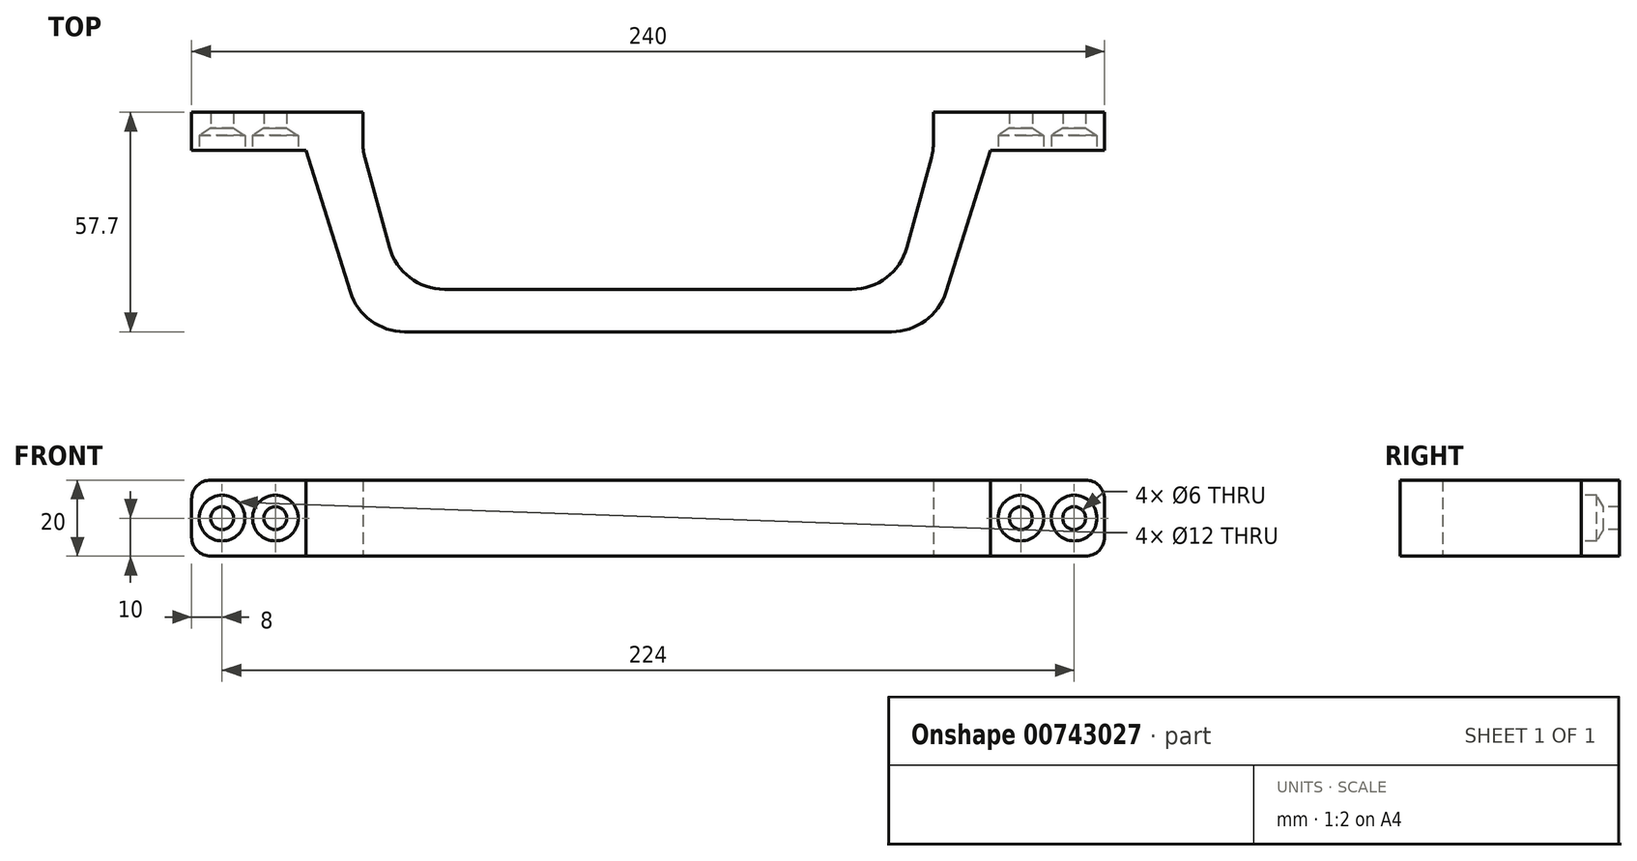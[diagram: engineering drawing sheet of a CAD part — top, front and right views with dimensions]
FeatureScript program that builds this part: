
annotation { "Feature Type Name" : "Feature", "Feature Type Description" : "" }
export const myFeature = defineFeature(function(context is Context, id is Id, definition is map)
    precondition{}
    {
        {
            var Q0;
            Q0=qCreatedBy(makeId("Top.planeOp"),FACE);
            var sketch = newSketch(context, id + "F0", { "sketchPlane" : qUnion([Q0])});
            skLineSegment(sketch, "E0.bottom", {"start": v(-120, 5) * mm, "end": v(120, 5) * mm});
            skLineSegment(sketch, "E0.top", {"start": v(-120, -5) * mm, "end": v(120, -5) * mm});
            skLineSegment(sketch, "E0.left", {"start": v(-120, 5) * mm, "end": v(-120, -5) * mm});
            skLineSegment(sketch, "E0.right", {"start": v(120, 5) * mm, "end": v(120, -5) * mm});
            skPoint(sketch, "E0.middle", {"position": v(0, 0) * mm});
            skLineSegment(sketch, "E1", {"start": v(-90, 5) * mm, "end": v(-90, -5) * mm});
            skLineSegment(sketch, "E2", {"start": v(90, -5) * mm, "end": v(90, 5) * mm});
            skLineSegment(sketch, "E3", {"start": v(-75, 5) * mm, "end": v(-75, -5) * mm});
            skLineSegment(sketch, "E4", {"start": v(75, 5) * mm, "end": v(75, -5) * mm});
            skLineSegment(sketch, "E5", {"start": v(-90, -5) * mm, "end": v(-75, -52.7) * mm});
            skLineSegment(sketch, "E6", {"start": v(-75, -52.7) * mm, "end": v(75, -52.7) * mm});
            skLineSegment(sketch, "E7", {"start": v(75, -52.7) * mm, "end": v(90, -5) * mm});
            skLineSegment(sketch, "E8", {"start": v(-75, -5) * mm, "end": v(-65, -41.52) * mm});
            skLineSegment(sketch, "E9", {"start": v(-65, -41.52) * mm, "end": v(65, -41.52) * mm});
            skLineSegment(sketch, "E10", {"start": v(65, -41.52) * mm, "end": v(75, -5) * mm});
            skSolve(sketch);
        }
        {
            var Q0;
            {var subQ0=sQuery(id+"F0.wireOp",EDGE,"E0.left");Q0=makeQuery(id+"F0.imprint","IMPRINT",FACE,{"disambiguationData":[TD([[makeQuery(id+"F0.imprint","IMPRINT",EDGE,{"derivedFrom":subQ0}),1.0]])]});}
            var Q1;
            {var subQ0=sQuery(id+"F0.wireOp",EDGE,"E1");Q1=makeQuery(id+"F0.imprint","IMPRINT",FACE,{"disambiguationData":[TD([[makeQuery(id+"F0.imprint","IMPRINT",EDGE,{"derivedFrom":subQ0}),1.0]])]});}
            var Q2;
            {var subQ0=sQuery(id+"F0.wireOp",EDGE,"E5");Q2=makeQuery(id+"F0.imprint","IMPRINT",FACE,{"disambiguationData":[TD([[makeQuery(id+"F0.imprint","IMPRINT",EDGE,{"derivedFrom":subQ0}),1.0]])]});}
            var Q3;
            {var subQ0=sQuery(id+"F0.wireOp",EDGE,"E2");Q3=makeQuery(id+"F0.imprint","IMPRINT",FACE,{"disambiguationData":[TD([[makeQuery(id+"F0.imprint","IMPRINT",EDGE,{"derivedFrom":subQ0}),1.0]])]});}
            var Q4;
            {var subQ0=sQuery(id+"F0.wireOp",EDGE,"E0.right");Q4=makeQuery(id+"F0.imprint","IMPRINT",FACE,{"disambiguationData":[TD([[makeQuery(id+"F0.imprint","IMPRINT",EDGE,{"derivedFrom":subQ0}),-1.0]])]});}
            extrude(context, id + "F1", {"entities" : qUnion([Q0, Q1, Q2, Q3, Q4]), "depth" : 20 * mm, "offsetDistance" : 25 * mm});
        }
        {
            var Q0;
            {var subQ0=sQuery(id+"F0.wireOp",EDGE,"E0.top");Q0=makeQuery(id+"F1.opExtrude","SWEPT_FACE",FACE,{"disambiguationData":[OSD([subQ0]),TDD([makeQuery(id+"F0.imprint","IMPRINT",EDGE,{"disambiguationData":[TD([[makeQuery(id+"F0.imprint","INTERSECT",VERTEX,{"derivedFrom":[subQ0,sQuery(id+"F0.wireOp",EDGE,"E0.left")]}),-1.0]])],"derivedFrom":subQ0})])]});}
            var sketch = newSketch(context, id + "F2", { "sketchPlane" : qUnion([Q0])});
            skCircle(sketch, "E11", {"center": v(-98, 10) * mm, "radius": 6 * mm});
            skCircle(sketch, "E12", {"center": v(-112, 10) * mm, "radius": 6 * mm});
            skCircle(sketch, "E13", {"center": v(98, 10) * mm, "radius": 6 * mm});
            skCircle(sketch, "E14", {"center": v(112, 10) * mm, "radius": 6 * mm});
            skSolve(sketch);
        }
        {
            var Q0;
            Q0=sQuery(id+"F2.wireOp",VERTEX,"E12.center");
            var Q1;
            Q1=sQuery(id+"F2.wireOp",VERTEX,"E11.center");
            var Q2;
            Q2=sQuery(id+"F2.wireOp",VERTEX,"E13.center");
            var Q3;
            Q3=sQuery(id+"F2.wireOp",VERTEX,"E14.center");
            var Q4;
            Q4=makeQuery(id+"F1.opExtrude","SWEPT_BODY",BODY,{"disambiguationData":[OSD([sQuery(id+"F0.wireOp",EDGE,"E0.bottom"),sQuery(id+"F0.wireOp",EDGE,"E0.top"),sQuery(id+"F0.wireOp",EDGE,"E0.left"),sQuery(id+"F0.wireOp",EDGE,"E0.right"),sQuery(id+"F0.wireOp",EDGE,"E3"),sQuery(id+"F0.wireOp",EDGE,"E4"),sQuery(id+"F0.wireOp",EDGE,"E5"),sQuery(id+"F0.wireOp",EDGE,"E6"),sQuery(id+"F0.wireOp",EDGE,"E7"),sQuery(id+"F0.wireOp",EDGE,"E8"),sQuery(id+"F0.wireOp",EDGE,"E9"),sQuery(id+"F0.wireOp",EDGE,"E10")])]});
            hole(context, id + "F3", {"style" : HoleStyle.SIMPLE, "endStyle" : HoleEndStyle.THROUGH, "holeDiameter" : 6 * mm, "majorDiameter" : 5 * mm, "isTappedThrough" : true, "tappedDepth" : 12 * mm, "tapClearance" : 3, "startFromSketch" : true, "locations" : qUnion([Q0, Q1, Q2, Q3]), "scope" : qUnion([Q4])});
        }
        {
            var Q0;
            Q0=sQuery(id+"F2.wireOp",VERTEX,"E12.center");
            var Q1;
            Q1=sQuery(id+"F2.wireOp",VERTEX,"E11.center");
            var Q2;
            Q2=sQuery(id+"F2.wireOp",VERTEX,"E13.center");
            var Q3;
            Q3=sQuery(id+"F2.wireOp",VERTEX,"E14.center");
            var Q4;
            Q4=makeQuery(id+"F1.opExtrude","SWEPT_BODY",BODY,{"disambiguationData":[OSD([sQuery(id+"F0.wireOp",EDGE,"E0.bottom"),sQuery(id+"F0.wireOp",EDGE,"E0.top"),sQuery(id+"F0.wireOp",EDGE,"E0.left"),sQuery(id+"F0.wireOp",EDGE,"E0.right"),sQuery(id+"F0.wireOp",EDGE,"E3"),sQuery(id+"F0.wireOp",EDGE,"E4"),sQuery(id+"F0.wireOp",EDGE,"E5"),sQuery(id+"F0.wireOp",EDGE,"E6"),sQuery(id+"F0.wireOp",EDGE,"E7"),sQuery(id+"F0.wireOp",EDGE,"E8"),sQuery(id+"F0.wireOp",EDGE,"E9"),sQuery(id+"F0.wireOp",EDGE,"E10")])]});
            hole(context, id + "F4", {"style" : HoleStyle.SIMPLE, "endStyle" : HoleEndStyle.BLIND, "holeDiameter" : 12 * mm, "majorDiameter" : 5 * mm, "holeDepth" : 4 * mm, "isTappedThrough" : true, "tappedDepth" : 12 * mm, "tapClearance" : 3, "startFromSketch" : true, "locations" : qUnion([Q0, Q1, Q2, Q3]), "scope" : qUnion([Q4])});
        }
        {
            var Q0;
            Q0=makeQuery(id+"F1.opExtrude","CAP_EDGE",EDGE,{"disambiguationData":[OSD([sQuery(id+"F0.wireOp",EDGE,"E0.left")])],"isStart":false});
            var Q1;
            Q1=makeQuery(id+"F1.opExtrude","CAP_EDGE",EDGE,{"disambiguationData":[OSD([sQuery(id+"F0.wireOp",EDGE,"E0.left")])],"isStart":true});
            var Q2;
            Q2=makeQuery(id+"F1.opExtrude","CAP_EDGE",EDGE,{"disambiguationData":[OSD([sQuery(id+"F0.wireOp",EDGE,"E0.right")])],"isStart":false});
            var Q3;
            Q3=makeQuery(id+"F1.opExtrude","CAP_EDGE",EDGE,{"disambiguationData":[OSD([sQuery(id+"F0.wireOp",EDGE,"E0.right")])],"isStart":true});
            fillet(context, id + "F5", {"entities" : qUnion([Q0, Q1, Q2, Q3]), "radius" : 5 * mm, "tangentPropagation" : true, "allowEdgeOverflow" : false});
        }
        {
            var Q0;
            Q0=makeQuery(id+"F1.opExtrude","SWEPT_EDGE",EDGE,{"disambiguationData":[OSD([sQuery(id+"F0.wireOp",EDGE,"E5"),sQuery(id+"F0.wireOp",EDGE,"E6")])]});
            var Q1;
            Q1=makeQuery(id+"F1.opExtrude","SWEPT_EDGE",EDGE,{"disambiguationData":[OSD([sQuery(id+"F0.wireOp",EDGE,"E6"),sQuery(id+"F0.wireOp",EDGE,"E7")])]});
            var Q2;
            Q2=makeQuery(id+"F1.opExtrude","SWEPT_EDGE",EDGE,{"disambiguationData":[OSD([sQuery(id+"F0.wireOp",EDGE,"E8"),sQuery(id+"F0.wireOp",EDGE,"E9")])]});
            var Q3;
            Q3=makeQuery(id+"F1.opExtrude","SWEPT_EDGE",EDGE,{"disambiguationData":[OSD([sQuery(id+"F0.wireOp",EDGE,"E9"),sQuery(id+"F0.wireOp",EDGE,"E10")])]});
            var Q4;
            Q4=makeQuery(id+"F1.opExtrude","SWEPT_EDGE",EDGE,{"disambiguationData":[OSD([sQuery(id+"F0.wireOp",EDGE,"E0.top"),sQuery(id+"F0.wireOp",EDGE,"E3"),sQuery(id+"F0.wireOp",EDGE,"E8")])]});
            var Q5;
            Q5=makeQuery(id+"F1.opExtrude","SWEPT_EDGE",EDGE,{"disambiguationData":[OSD([sQuery(id+"F0.wireOp",EDGE,"E0.top"),sQuery(id+"F0.wireOp",EDGE,"E4"),sQuery(id+"F0.wireOp",EDGE,"E10")])]});
            fillet(context, id + "F6", {"entities" : qUnion([Q0, Q1, Q2, Q3, Q4, Q5]), "radius" : 15 * mm, "tangentPropagation" : true, "allowEdgeOverflow" : false});
        }
    });
